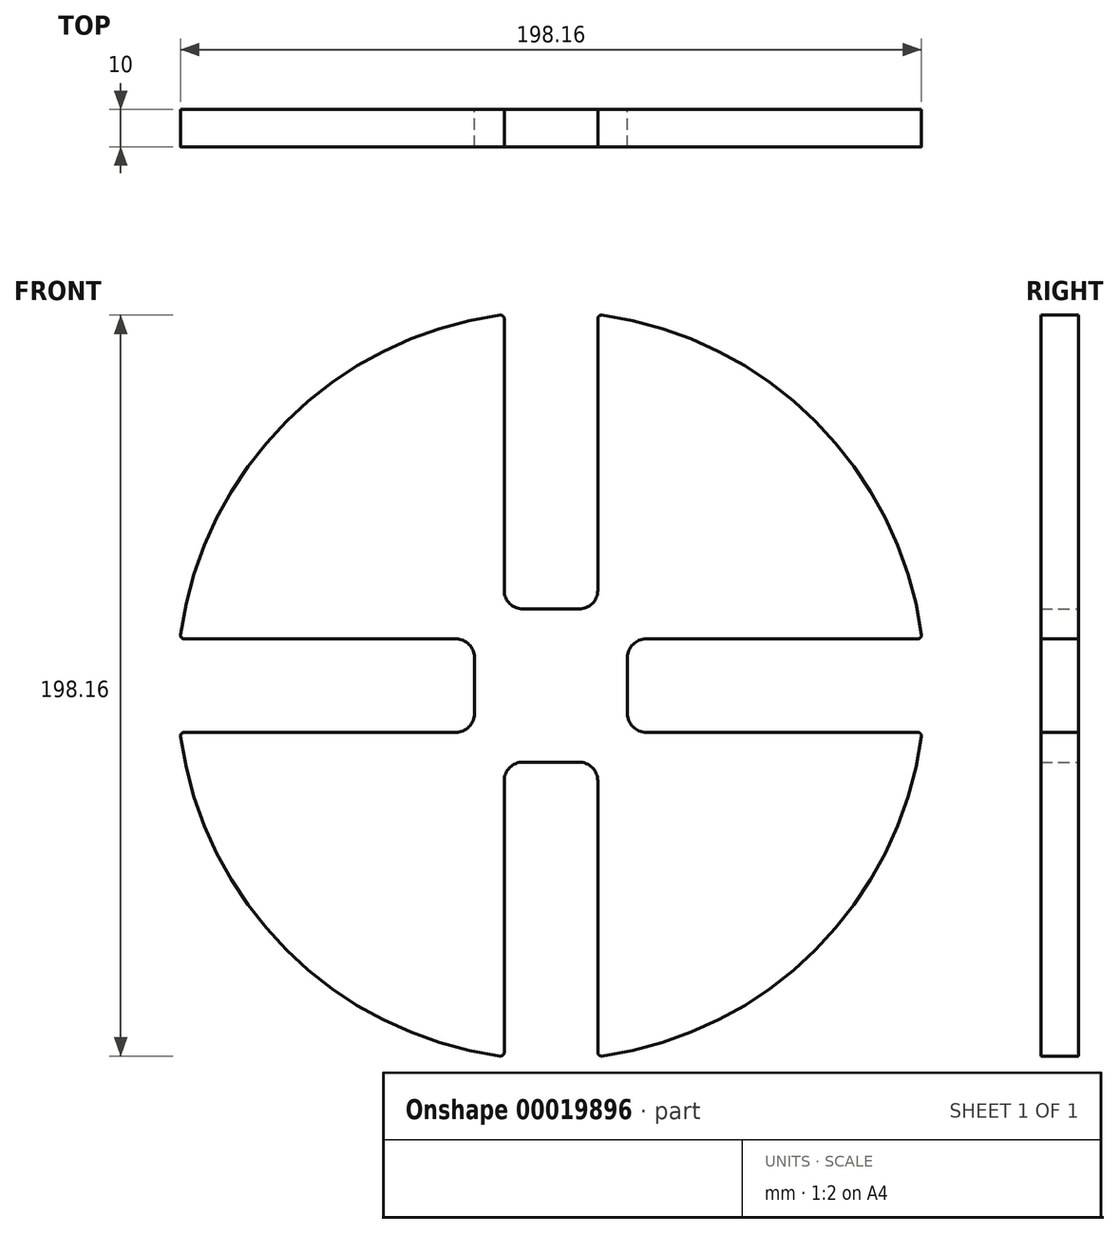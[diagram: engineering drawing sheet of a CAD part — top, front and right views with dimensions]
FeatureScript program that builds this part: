
annotation { "Feature Type Name" : "Feature", "Feature Type Description" : "" }
export const myFeature = defineFeature(function(context is Context, id is Id, definition is map)
    precondition{}
    {
        {
            var Q0;
            Q0=qCreatedBy(makeId("Front.planeOp"),FACE);
            var sketch = newSketch(context, id + "F0", { "sketchPlane" : qUnion([Q0])});
            skArc(sketch, "E0", {"start": v(-12.5, 99.22) * mm, "mid": v(-70.71, 70.71) * mm, "end": v(-99.22, 12.5) * mm});
            skLineSegment(sketch, "E1", {"start": v(99.22, -12.5) * mm, "end": v(20.47, -12.5) * mm});
            skLineSegment(sketch, "E2", {"start": v(20.47, -12.5) * mm, "end": v(20.47, 12.5) * mm});
            skLineSegment(sketch, "E3", {"start": v(20.47, 12.5) * mm, "end": v(99.22, 12.5) * mm});
            skLineSegment(sketch, "E4.1.0", {"start": v(-12.5, 20.47) * mm, "end": v(-12.5, 99.22) * mm});
            skLineSegment(sketch, "E4.1.1", {"start": v(12.5, 20.47) * mm, "end": v(-12.5, 20.47) * mm});
            skLineSegment(sketch, "E4.1.2", {"start": v(12.5, 99.22) * mm, "end": v(12.5, 20.47) * mm});
            skLineSegment(sketch, "E4.2.0", {"start": v(-20.47, -12.5) * mm, "end": v(-99.22, -12.5) * mm});
            skLineSegment(sketch, "E4.2.1", {"start": v(-20.47, 12.5) * mm, "end": v(-20.47, -12.5) * mm});
            skLineSegment(sketch, "E4.2.2", {"start": v(-99.22, 12.5) * mm, "end": v(-20.47, 12.5) * mm});
            skLineSegment(sketch, "E4.3.0", {"start": v(12.5, -20.47) * mm, "end": v(12.5, -99.22) * mm});
            skLineSegment(sketch, "E4.3.1", {"start": v(-12.5, -20.47) * mm, "end": v(12.5, -20.47) * mm});
            skLineSegment(sketch, "E4.3.2", {"start": v(-12.5, -99.22) * mm, "end": v(-12.5, -20.47) * mm});
            skArc(sketch, "E5.trimOffspring", {"start": v(99.22, 12.5) * mm, "mid": v(70.71, 70.71) * mm, "end": v(12.5, 99.22) * mm});
            skArc(sketch, "E6.trimOffspring", {"start": v(12.5, -99.22) * mm, "mid": v(70.71, -70.71) * mm, "end": v(99.22, -12.5) * mm});
            skArc(sketch, "E7.trimOffspring", {"start": v(-99.22, -12.5) * mm, "mid": v(-70.71, -70.71) * mm, "end": v(-12.5, -99.22) * mm});
            skPoint(sketch, "E8", {"position": v(-50, 50) * mm});
            skPoint(sketch, "E9", {"position": v(0, 97.23) * mm});
            skPoint(sketch, "E10", {"position": v(0, -91.28) * mm});
            skPoint(sketch, "E11", {"position": v(96.48, 0) * mm});
            skPoint(sketch, "E12", {"position": v(-100.95, 0) * mm});
            skLineSegment(sketch, "E13", {"start": v(-100.95, 0) * mm, "end": v(96.48, 0) * mm, "construction": true});
            skLineSegment(sketch, "E14", {"start": v(0, 97.23) * mm, "end": v(0, -91.28) * mm, "construction": true});
            skPoint(sketch, "E15.MirrorP", {"position": v(50, 50) * mm});
            skPoint(sketch, "E16.MirrorP", {"position": v(-50, -50) * mm});
            skPoint(sketch, "E17.MirrorP", {"position": v(50, -50) * mm});
            skSolve(sketch);
        }
        {
            var Q0;
            Q0=makeQuery(id+"F0.imprint","IMPRINT",FACE,{"disambiguationData":[TD([[makeQuery(id+"F0.imprint","IMPRINT",EDGE,{"derivedFrom":sQuery(id+"F0.wireOp",EDGE,"E0")}),1.0]])]});
            extrude(context, id + "F1", {"entities" : qUnion([Q0]), "depth" : 10 * mm});
        }
        {
            var Q0;
            Q0=makeQuery(id+"F1.opExtrude","SWEPT_EDGE",EDGE,{"disambiguationData":[OSD([sQuery(id+"F0.wireOp",EDGE,"E0"),sQuery(id+"F0.wireOp",EDGE,"E4.1.0")])]});
            var Q1;
            Q1=makeQuery(id+"F1.opExtrude","SWEPT_EDGE",EDGE,{"disambiguationData":[OSD([sQuery(id+"F0.wireOp",EDGE,"E4.1.2"),sQuery(id+"F0.wireOp",EDGE,"E5.trimOffspring")])]});
            var Q2;
            Q2=makeQuery(id+"F1.opExtrude","SWEPT_EDGE",EDGE,{"disambiguationData":[OSD([sQuery(id+"F0.wireOp",EDGE,"E1"),sQuery(id+"F0.wireOp",EDGE,"E6.trimOffspring")])]});
            var Q3;
            Q3=makeQuery(id+"F1.opExtrude","SWEPT_EDGE",EDGE,{"disambiguationData":[OSD([sQuery(id+"F0.wireOp",EDGE,"E4.2.0"),sQuery(id+"F0.wireOp",EDGE,"E7.trimOffspring")])]});
            var Q4;
            Q4=makeQuery(id+"F1.opExtrude","SWEPT_EDGE",EDGE,{"disambiguationData":[OSD([sQuery(id+"F0.wireOp",EDGE,"E4.3.2"),sQuery(id+"F0.wireOp",EDGE,"E7.trimOffspring")])]});
            var Q5;
            Q5=makeQuery(id+"F1.opExtrude","SWEPT_EDGE",EDGE,{"disambiguationData":[OSD([sQuery(id+"F0.wireOp",EDGE,"E4.3.0"),sQuery(id+"F0.wireOp",EDGE,"E6.trimOffspring")])]});
            var Q6;
            Q6=makeQuery(id+"F1.opExtrude","SWEPT_EDGE",EDGE,{"disambiguationData":[OSD([sQuery(id+"F0.wireOp",EDGE,"E0"),sQuery(id+"F0.wireOp",EDGE,"E4.2.2")])]});
            var Q7;
            Q7=makeQuery(id+"F1.opExtrude","SWEPT_EDGE",EDGE,{"disambiguationData":[OSD([sQuery(id+"F0.wireOp",EDGE,"E3"),sQuery(id+"F0.wireOp",EDGE,"E5.trimOffspring")])]});
            fillet(context, id + "F2", {"entities" : qUnion([Q0, Q1, Q2, Q3, Q4, Q5, Q6, Q7]), "radius" : 1 * mm, "tangentPropagation" : true, "allowEdgeOverflow" : false});
        }
        {
            var Q0;
            Q0=makeQuery(id+"F1.opExtrude","SWEPT_EDGE",EDGE,{"disambiguationData":[OSD([sQuery(id+"F0.wireOp",EDGE,"E4.1.0"),sQuery(id+"F0.wireOp",EDGE,"E4.1.1")])]});
            var Q1;
            Q1=makeQuery(id+"F1.opExtrude","SWEPT_EDGE",EDGE,{"disambiguationData":[OSD([sQuery(id+"F0.wireOp",EDGE,"E1"),sQuery(id+"F0.wireOp",EDGE,"E2")])]});
            var Q2;
            Q2=makeQuery(id+"F1.opExtrude","SWEPT_EDGE",EDGE,{"disambiguationData":[OSD([sQuery(id+"F0.wireOp",EDGE,"E4.1.1"),sQuery(id+"F0.wireOp",EDGE,"E4.1.2")])]});
            var Q3;
            Q3=makeQuery(id+"F1.opExtrude","SWEPT_EDGE",EDGE,{"disambiguationData":[OSD([sQuery(id+"F0.wireOp",EDGE,"E4.2.0"),sQuery(id+"F0.wireOp",EDGE,"E4.2.1")])]});
            var Q4;
            Q4=makeQuery(id+"F1.opExtrude","SWEPT_EDGE",EDGE,{"disambiguationData":[OSD([sQuery(id+"F0.wireOp",EDGE,"E4.2.1"),sQuery(id+"F0.wireOp",EDGE,"E4.2.2")])]});
            var Q5;
            Q5=makeQuery(id+"F1.opExtrude","SWEPT_EDGE",EDGE,{"disambiguationData":[OSD([sQuery(id+"F0.wireOp",EDGE,"E2"),sQuery(id+"F0.wireOp",EDGE,"E3")])]});
            var Q6;
            Q6=makeQuery(id+"F1.opExtrude","SWEPT_EDGE",EDGE,{"disambiguationData":[OSD([sQuery(id+"F0.wireOp",EDGE,"E4.3.1"),sQuery(id+"F0.wireOp",EDGE,"E4.3.2")])]});
            var Q7;
            Q7=makeQuery(id+"F1.opExtrude","SWEPT_EDGE",EDGE,{"disambiguationData":[OSD([sQuery(id+"F0.wireOp",EDGE,"E4.3.0"),sQuery(id+"F0.wireOp",EDGE,"E4.3.1")])]});
            fillet(context, id + "F3", {"entities" : qUnion([Q0, Q1, Q2, Q3, Q4, Q5, Q6, Q7]), "radius" : 5 * mm, "tangentPropagation" : true, "allowEdgeOverflow" : false});
        }
    });
